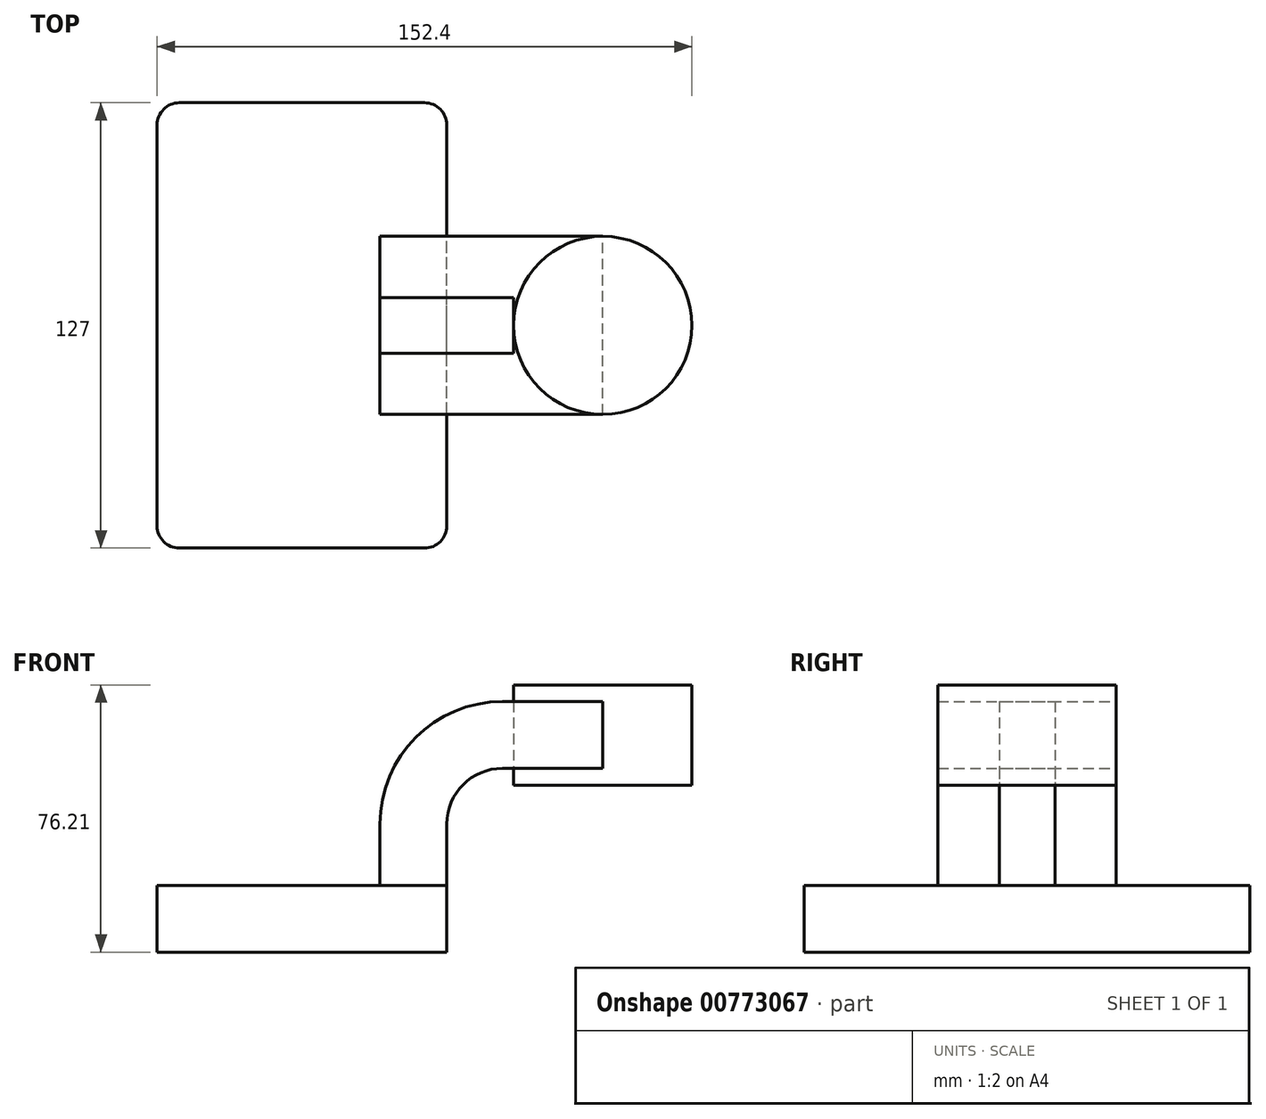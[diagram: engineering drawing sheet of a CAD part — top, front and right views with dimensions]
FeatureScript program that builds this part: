
annotation { "Feature Type Name" : "Feature", "Feature Type Description" : "" }
export const myFeature = defineFeature(function(context is Context, id is Id, definition is map)
    precondition{}
    {
        {
            var Q0;
            Q0=qCreatedBy(makeId("Front.planeOp"),FACE);
            var sketch = newSketch(context, id + "F0", { "sketchPlane" : qUnion([Q0])});
            skLineSegment(sketch, "E0.bottom", {"start": v(41.28, -9.52) * mm, "end": v(-41.28, -9.53) * mm});
            skLineSegment(sketch, "E0.top", {"start": v(41.28, 9.53) * mm, "end": v(-41.28, 9.53) * mm});
            skLineSegment(sketch, "E0.left", {"start": v(41.28, -9.52) * mm, "end": v(41.28, 9.53) * mm});
            skLineSegment(sketch, "E0.right", {"start": v(-41.28, -9.53) * mm, "end": v(-41.28, 9.53) * mm});
            skPoint(sketch, "E0.middle", {"position": v(0, 0) * mm});
            skLineSegment(sketch, "E1.bottom", {"start": v(111.12, 66.68) * mm, "end": v(60.33, 66.68) * mm});
            skLineSegment(sketch, "E1.top", {"start": v(111.13, 38.1) * mm, "end": v(60.33, 38.1) * mm});
            skLineSegment(sketch, "E1.left", {"start": v(111.12, 66.68) * mm, "end": v(111.12, 38.1) * mm});
            skLineSegment(sketch, "E1.right", {"start": v(60.32, 66.68) * mm, "end": v(60.32, 38.1) * mm});
            skPoint(sketch, "E1.middle", {"position": v(85.73, 52.39) * mm});
            skLineSegment(sketch, "E2", {"start": v(41.28, 9.53) * mm, "end": v(41.28, 27) * mm});
            skArc(sketch, "E3", {"start": v(41.27, 27) * mm, "mid": v(45.92, 38.23) * mm, "end": v(57.15, 42.88) * mm});
            skLineSegment(sketch, "E4", {"start": v(57.15, 42.88) * mm, "end": v(86, 42.88) * mm});
            skLineSegment(sketch, "E5.0", {"start": v(41.31, 9.53) * mm, "end": v(41.31, 27) * mm});
            skLineSegment(sketch, "E6.0", {"start": v(57.15, 61.93) * mm, "end": v(86, 61.93) * mm});
            skArc(sketch, "E6.1", {"start": v(22.23, 27) * mm, "mid": v(32.45, 51.7) * mm, "end": v(57.15, 61.93) * mm});
            skLineSegment(sketch, "E6.2", {"start": v(22.22, 9.53) * mm, "end": v(22.22, 27) * mm});
            skFitSpline(sketch, "E7", {"points": [v(-41.28, 9.53) * mm, v(57.15, 61.93) * mm], "startDerivative": vector(62.16, 105.24) * mm, "endDerivative": vector(123.82, -5.78) * mm});
            skLineSegment(sketch, "E8", {"start": v(85.72, 38.1) * mm, "end": v(85.72, 66.68) * mm});
            skSolve(sketch);
        }
        {
            var Q0;
            Q0=makeQuery(id+"F0.imprint","IMPRINT",FACE,{"disambiguationData":[TD([[makeQuery(id+"F0.imprint","IMPRINT",EDGE,{"derivedFrom":sQuery(id+"F0.wireOp",EDGE,"E0.bottom")}),-1.0]])]});
            extrude(context, id + "F1", {"entities" : qUnion([Q0]), "endBound" : BoundingType.SYMMETRIC, "depth" : 127 * mm, "offsetDistance" : 25.4 * mm});
        }
        {
            var Q0;
            {var subQ1=sQuery(id+"F0.wireOp",EDGE,"E2");Q0=makeQuery(id+"F0.imprint","IMPRINT",FACE,{"disambiguationData":[TD([[makeQuery(id+"F0.imprint","IMPRINT",EDGE,{"derivedFrom":subQ1}),1.0]])]});}
            var Q1;
            {var subQ5=sQuery(id+"F0.wireOp",EDGE,"qHNoTIi8-5lvJ-BNJ3-ZNGQ-UmPzO8kYC6i6");Q1=makeQuery(id+"F0.imprint","IMPRINT",FACE,{"disambiguationData":[TD([[makeQuery(id+"F0.imprint","IMPRINT",EDGE,{"derivedFrom":subQ5}),1.0]])]});}
            var Q2;
            {var subQ0=sQuery(id+"F0.wireOp",EDGE,"E6.0");var subQ1=sQuery(id+"F0.wireOp",EDGE,"E1.right");var subQ2=makeQuery(id+"F0.imprint","INTERSECT",VERTEX,{"derivedFrom":[subQ1,subQ0]});Q2=makeQuery(id+"F0.imprint","IMPRINT",FACE,{"disambiguationData":[TD([[makeQuery(id+"F0.imprint","IMPRINT",EDGE,{"disambiguationData":[TD([[subQ2,-1.0]])],"derivedFrom":subQ1}),1.0]])]});}
            extrude(context, id + "F2", {"entities" : qUnion([Q0, Q1, Q2]), "endBound" : BoundingType.SYMMETRIC, "depth" : 50.8 * mm, "offsetDistance" : 25.4 * mm});
        }
        {
            var Q0;
            Q0=makeQuery(id+"F0.imprint","IMPRINT",FACE,{"disambiguationData":[TD([[makeQuery(id+"F0.imprint","IMPRINT",EDGE,{"derivedFrom":sQuery(id+"F0.wireOp",EDGE,"E6.1")}),1.0]])]});
            extrude(context, id + "F3", {"entities" : qUnion([Q0]), "endBound" : BoundingType.SYMMETRIC, "depth" : 15.88 * mm, "offsetDistance" : 25.4 * mm});
        }
        {
            var Q0;
            {var subQ0=sQuery(id+"F0.wireOp",EDGE,"E1.left");Q0=makeQuery(id+"F0.imprint","IMPRINT",FACE,{"disambiguationData":[TD([[makeQuery(id+"F0.imprint","IMPRINT",EDGE,{"derivedFrom":subQ0}),-1.0]])]});}
            var Q1;
            Q1=sQuery(id+"F0.wireOp",EDGE,"E8");
            revolve(context, id + "F4", {"surfaceOperationType" : NewSurfaceOperationType.NEW, "entities" : qUnion([Q0]), "axis" : qUnion([Q1]), "revolveType" : RevolveType.FULL});
        }
        {
            var Q0;
            Q0=makeQuery(id+"F1.opExtrude","CAP_EDGE",EDGE,{"disambiguationData":[OSD([sQuery(id+"F0.wireOp",EDGE,"E0.left")])],"isStart":false});
            var Q1;
            Q1=makeQuery(id+"F1.opExtrude","CAP_EDGE",EDGE,{"disambiguationData":[OSD([sQuery(id+"F0.wireOp",EDGE,"E0.right")])],"isStart":false});
            var Q2;
            Q2=makeQuery(id+"F1.opExtrude","CAP_EDGE",EDGE,{"disambiguationData":[OSD([sQuery(id+"F0.wireOp",EDGE,"E0.left")])],"isStart":true});
            var Q3;
            Q3=makeQuery(id+"F1.opExtrude","CAP_EDGE",EDGE,{"disambiguationData":[OSD([sQuery(id+"F0.wireOp",EDGE,"E0.right")])],"isStart":true});
            fillet(context, id + "F5", {"entities" : qUnion([Q0, Q1, Q2, Q3]), "radius" : 6.35 * mm, "tangentPropagation" : true, "allowEdgeOverflow" : false});
        }
    });
